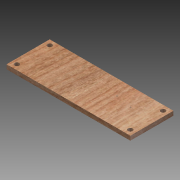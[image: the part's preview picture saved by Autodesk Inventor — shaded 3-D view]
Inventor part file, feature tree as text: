
AUTODESK INVENTOR PART (.ipt)
format: ipt  version: 2012 (Build 160160000, 160)  size: 98,816 bytes
history: native  units: mm
features: extrude x1, sketch x1
ambient origin geometry x8: Origin, YZ Plane, XZ Plane, XY Plane, X Axis, Y Axis, Z Axis, Center Point
bodies: Solid1 (feature_tree)
feature tree (2):
  extrude  "Extrusion1"  Depth=75.0mm
  sketch  "Sketch1"  dims[d0=215.0mm d1=75.0mm d2=8.0mm d3=9.0mm d4=9.0mm d5=9.0mm d6=9.0mm d7=9.0mm d8=9.0mm d9=9.0mm d10=9.0mm d11=7.5mm d12=0.0mm]
